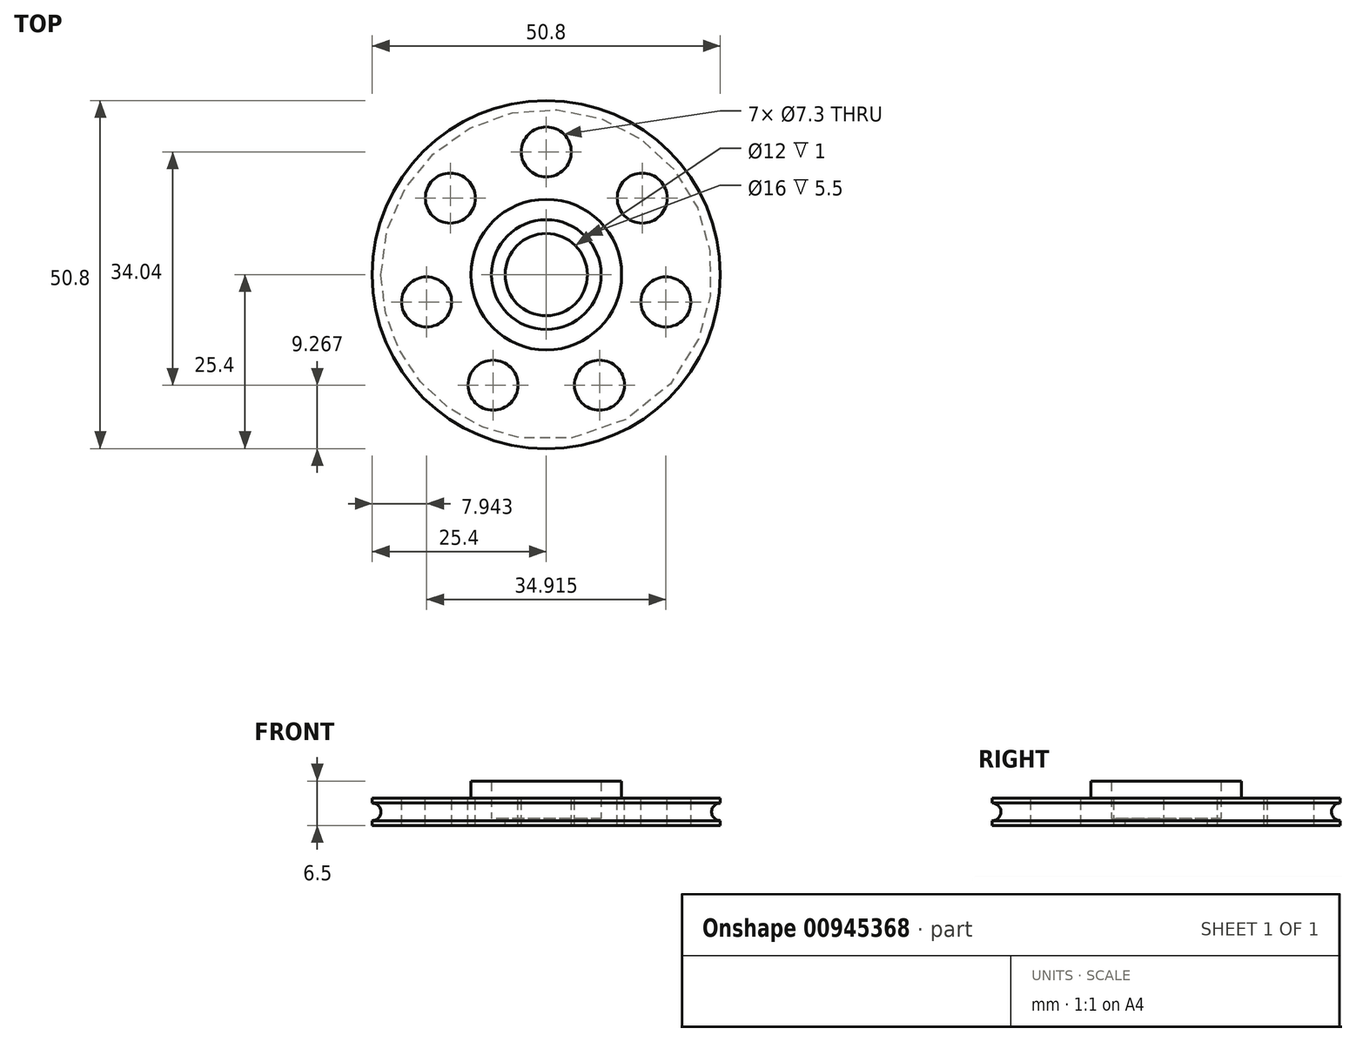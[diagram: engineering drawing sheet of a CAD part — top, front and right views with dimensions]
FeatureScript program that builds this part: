
annotation { "Feature Type Name" : "Feature", "Feature Type Description" : "" }
export const myFeature = defineFeature(function(context is Context, id is Id, definition is map)
    precondition{}
    {
        {
            var Q0;
            Q0=qCreatedBy(makeId("Top.planeOp"),FACE);
            var sketch = newSketch(context, id + "F0", { "sketchPlane" : qUnion([Q0])});
            skCircle(sketch, "E0", {"center": v(0, 0) * mm, "radius": 25.4 * mm});
            skSolve(sketch);
        }
        {
            var Q0;
            Q0=makeQuery(id+"F0.imprint","IMPRINT",FACE,{"disambiguationData":[TD([[makeQuery(id+"F0.imprint","IMPRINT",EDGE,{"derivedFrom":sQuery(id+"F0.wireOp",EDGE,"E0")}),1.0]])]});
            extrude(context, id + "F1", {"entities" : qUnion([Q0]), "depth" : 4 * mm, "offsetDistance" : 25.4 * mm});
        }
        {
            var Q0;
            Q0=makeQuery(id+"F1.opExtrude","CAP_FACE",FACE,{"disambiguationData":[OSD([sQuery(id+"F0.wireOp",EDGE,"E0"),sQuery(id+"F0.wireOp",EDGE,"n39IqKt5-bk1q-LU1x-fgod-8OyBNiFTd7FZ")])],"isStart":false});
            var sketch = newSketch(context, id + "F2", { "sketchPlane" : qUnion([Q0])});
            skCircle(sketch, "E1", {"center": v(0, 0) * mm, "radius": 8 * mm});
            skCircle(sketch, "E2.0", {"center": v(0, 0) * mm, "radius": 11 * mm});
            skSolve(sketch);
        }
        {
            var Q0;
            Q0=qSketchRegion(id+"F2",true);
            extrude(context, id + "F3", {"entities" : qUnion([Q0]), "operationType" : NewBodyOperationType.ADD, "flatOperationType" : FlatOperationType.REMOVE, "depth" : 2.5 * mm, "offsetDistance" : 25.4 * mm, "domain" : OperationDomain.MODEL});
        }
        {
            var Q0;
            Q0=makeQuery(id+"F3.boolean.opBoolean","SPLIT",FACE,{"disambiguationData":[TD([makeQuery(id+"F3.opExtrude","SWEPT_FACE",FACE,{"disambiguationData":[OSD([sQuery(id+"F2.wireOp",EDGE,"E1")])]})])],"derivedFrom":makeQuery(id+"F1.opExtrude","CAP_FACE",FACE,{"disambiguationData":[OSD([sQuery(id+"F0.wireOp",EDGE,"E0")])],"isStart":false})});
            var sketch = newSketch(context, id + "F4", { "sketchPlane" : qUnion([Q0])});
            skCircle(sketch, "E3", {"center": v(0, 0) * mm, "radius": 6 * mm});
            skSolve(sketch);
        }
        {
            var Q0;
            Q0=makeQuery(id+"F4.imprint","IMPRINT",FACE,{"disambiguationData":[TD([[makeQuery(id+"F4.imprint","IMPRINT",EDGE,{"derivedFrom":sQuery(id+"F4.wireOp",EDGE,"E3")}),1.0]])]});
            var Q1;
            Q1=makeQuery(id+"F4.imprint","IMPRINT",FACE,{"disambiguationData":[TD([[makeQuery(id+"F4.imprint","IMPRINT",EDGE,{"derivedFrom":makeQuery(id+"FgYK8jIepfClWtA_1.opExtrude","CAP_EDGE",EDGE,{"disambiguationData":[OSD([sQuery(id+"F8DXjnVyigKkjng_1.wireOp",EDGE,"EUjAMsCd-Zx2B-3j4q-cP5o-T3GrjTijNDqK")])],"isStart":false})}),1.0]])]});
            extrude(context, id + "F5", {"entities" : qUnion([Q0, Q1]), "operationType" : NewBodyOperationType.REMOVE, "oppositeDirection" : true, "depth" : 9 * mm, "offsetDistance" : 25.4 * mm});
        }
        {
            var Q0;
            Q0=qCreatedBy(makeId("Front.planeOp"),FACE);
            var sketch = newSketch(context, id + "F6", { "sketchPlane" : qUnion([Q0])});
            skCircle(sketch, "E4", {"center": v(-27.3, 2) * mm, "radius": 1.5 * mm});
            skLineSegment(sketch, "E5.bottom", {"start": v(-25.8, 0.65) * mm, "end": v(-27.95, 0.65) * mm});
            skLineSegment(sketch, "E5.top", {"start": v(-25.8, 3.35) * mm, "end": v(-27.95, 3.35) * mm});
            skLineSegment(sketch, "E5.left", {"start": v(-25.8, 0.65) * mm, "end": v(-25.8, 3.35) * mm});
            skLineSegment(sketch, "E5.right", {"start": v(-28.8, 1.91) * mm, "end": v(-28.8, 2.09) * mm});
            skLineSegment(sketch, "E6", {"start": v(0, 19.1) * mm, "end": v(0, -12.61) * mm, "construction": true});
            skLineSegment(sketch, "E7", {"start": v(-25.8, 1.83) * mm, "end": v(-25.81, 1.83) * mm});
            skPoint(sketch, "E8.orphan", {"position": v(-38.97, 3.35) * mm});
            skPoint(sketch, "E9.end.orphan", {"position": v(-15.64, 0.65) * mm});
            skPoint(sketch, "E9.start.orphan", {"position": v(-25.8, 2) * mm});
            skSolve(sketch);
        }
        {
            var Q0;
            {var subQ0=sQuery(id+"F6.wireOp",EDGE,"E5.top");var subQ1=sQuery(id+"F6.wireOp",EDGE,"E4");var subQ2=makeQuery(id+"F6.imprint","INTERSECT",VERTEX,{"disambiguationData":[OD(0.0)],"derivedFrom":[subQ1,subQ0]});Q0=makeQuery(id+"F6.imprint","IMPRINT",FACE,{"disambiguationData":[TD([[makeQuery(id+"F6.imprint","IMPRINT",EDGE,{"disambiguationData":[TD([[subQ2,1.0]])],"derivedFrom":subQ1}),1.0]])]});}
            var Q1;
            {var subQ0=sQuery(id+"F6.wireOp",EDGE,"E5.bottom");var subQ1=sQuery(id+"F6.wireOp",EDGE,"E4");var subQ2=makeQuery(id+"F6.imprint","INTERSECT",VERTEX,{"disambiguationData":[OD(0.0)],"derivedFrom":[subQ1,subQ0]});Q1=makeQuery(id+"F6.imprint","IMPRINT",FACE,{"disambiguationData":[TD([[makeQuery(id+"F6.imprint","IMPRINT",EDGE,{"disambiguationData":[TD([[subQ2,-1.0]])],"derivedFrom":subQ1}),1.0]])]});}
            var Q2;
            {var subQ4=sQuery(id+"F6.wireOp",EDGE,"E5.right");Q2=makeQuery(id+"F6.imprint","IMPRINT",FACE,{"disambiguationData":[TD([[makeQuery(id+"F6.imprint","IMPRINT",EDGE,{"derivedFrom":subQ4}),-1.0]])]});}
            var Q3;
            {var subQ0=sQuery(id+"F6.wireOp",EDGE,"p3G3spWP-JurA-dj01-Cwvm-HHlCDoPDIoxd");Q3=makeQuery(id+"F6.imprint","IMPRINT",FACE,{"disambiguationData":[TD([[makeQuery(id+"F6.imprint","IMPRINT",EDGE,{"derivedFrom":subQ0}),1.0]])]});}
            var Q4;
            Q4=makeQuery(id+"F6.imprint","IMPRINT",FACE,{"disambiguationData":[TD([[makeQuery(id+"F6.imprint","IMPRINT",EDGE,{"derivedFrom":sQuery(id+"F6.wireOp",EDGE,"p3G3spWP-JurA-dj01-Cwvm-HHlCDoPDIoxd")}),-1.0]])]});
            var Q5;
            {var subQ0=sQuery(id+"F6.wireOp",EDGE,"E9");Q5=makeQuery(id+"F6.imprint","IMPRINT",FACE,{"disambiguationData":[TD([[makeQuery(id+"F6.imprint","IMPRINT",EDGE,{"derivedFrom":subQ0}),1.0]])]});}
            var Q6;
            Q6=sQuery(id+"F6.wireOp",EDGE,"E6");
            revolve(context, id + "F7", {"operationType" : NewBodyOperationType.REMOVE, "surfaceOperationType" : NewSurfaceOperationType.NEW, "entities" : qUnion([Q0, Q1, Q2, Q3, Q4, Q5]), "axis" : qUnion([Q6]), "revolveType" : RevolveType.FULL, "oppositeDirection" : true});
        }
        {
            var Q0;
            Q0=makeQuery(id+"F3.boolean.opBoolean","SPLIT",FACE,{"disambiguationData":[TD([makeQuery(id+"F3.opExtrude","SWEPT_FACE",FACE,{"disambiguationData":[OSD([sQuery(id+"F2.wireOp",EDGE,"E1")])]})])],"derivedFrom":makeQuery(id+"F1.opExtrude","CAP_FACE",FACE,{"disambiguationData":[OSD([sQuery(id+"F0.wireOp",EDGE,"E0")])],"isStart":false})});
            extrude(context, id + "F8", {"entities" : qUnion([Q0]), "operationType" : NewBodyOperationType.REMOVE, "oppositeDirection" : true, "depth" : 3 * mm, "offsetDistance" : 25 * mm});
        }
        {
            var Q0;
            Q0=qCreatedBy(makeId("Front.planeOp"),FACE);
            var sketch = newSketch(context, id + "F9", { "sketchPlane" : qUnion([Q0])});
            skLineSegment(sketch, "E10", {"start": v(-25.4, 4) * mm, "end": v(-25.4, 0) * mm});
            skCircle(sketch, "E11", {"center": v(-25.4, 2) * mm, "radius": 1.28 * mm});
            skLineSegment(sketch, "E12", {"start": v(0, 9.34) * mm, "end": v(0, -3.6) * mm, "construction": true});
            skSolve(sketch);
        }
        {
            var Q0;
            {var subQ0=sQuery(id+"F9.wireOp",EDGE,"E11");var subQ1=sQuery(id+"F9.wireOp",EDGE,"E10");var subQ2=makeQuery(id+"F9.imprint","INTERSECT",VERTEX,{"disambiguationData":[OD(0.0)],"derivedFrom":[subQ1,subQ0]});Q0=makeQuery(id+"F9.imprint","IMPRINT",FACE,{"disambiguationData":[TD([[makeQuery(id+"F9.imprint","IMPRINT",EDGE,{"disambiguationData":[TD([[subQ2,1.0]])],"derivedFrom":subQ1}),1.0]])]});}
            var Q1;
            {var subQ0=sQuery(id+"F9.wireOp",EDGE,"E11");var subQ1=sQuery(id+"F9.wireOp",EDGE,"E10");var subQ2=makeQuery(id+"F9.imprint","INTERSECT",VERTEX,{"disambiguationData":[OD(0.0)],"derivedFrom":[subQ1,subQ0]});Q1=makeQuery(id+"F9.imprint","IMPRINT",FACE,{"disambiguationData":[TD([[makeQuery(id+"F9.imprint","IMPRINT",EDGE,{"disambiguationData":[TD([[subQ2,1.0]])],"derivedFrom":subQ1}),-1.0]])]});}
            var Q2;
            Q2=sQuery(id+"F9.wireOp",EDGE,"E12");
            revolve(context, id + "F10", {"operationType" : NewBodyOperationType.REMOVE, "surfaceOperationType" : NewSurfaceOperationType.NEW, "entities" : qUnion([Q0, Q1]), "axis" : qUnion([Q2]), "revolveType" : RevolveType.FULL, "oppositeDirection" : true});
        }
        {
            var Q0;
            {var subQ1=sQuery(id+"F0.wireOp",EDGE,"E0");var subQ2=makeQuery(id+"F1.opExtrude","SWEPT_FACE",FACE,{"disambiguationData":[OSD([subQ1])]});Q0=makeQuery(id+"FvaswZWDLJZ7FP9_1.boolean.opBoolean","SPLIT",FACE,{"disambiguationData":[TD([subQ2])],"derivedFrom":makeQuery(id+"F3.boolean.opBoolean","SPLIT",FACE,{"disambiguationData":[TD([subQ2])],"derivedFrom":makeQuery(id+"F1.opExtrude","CAP_FACE",FACE,{"disambiguationData":[OSD([subQ1])],"isStart":false})})});}
            var sketch = newSketch(context, id + "F11", { "sketchPlane" : qUnion([Q0])});
            skCircle(sketch, "E13", {"center": v(0, 17.9) * mm, "radius": 3.65 * mm});
            skCircle(sketch, "E14.1.0", {"center": v(-14, 11.16) * mm, "radius": 3.65 * mm});
            skCircle(sketch, "E14.2.0", {"center": v(-17.46, -3.98) * mm, "radius": 3.65 * mm});
            skCircle(sketch, "E14.3.0", {"center": v(-7.77, -16.13) * mm, "radius": 3.65 * mm});
            skCircle(sketch, "E14.4.0", {"center": v(7.77, -16.13) * mm, "radius": 3.65 * mm});
            skPoint(sketch, "E14.center", {"position": v(0, 0) * mm});
            skCircle(sketch, "E15.1.5.0", {"center": v(17.46, -3.98) * mm, "radius": 3.65 * mm});
            skCircle(sketch, "E15.1.6.0", {"center": v(14, 11.16) * mm, "radius": 3.65 * mm});
            skSolve(sketch);
        }
        {
            var Q0;
            Q0=makeQuery(id+"F11.imprint","IMPRINT",FACE,{"disambiguationData":[TD([[makeQuery(id+"F11.imprint","IMPRINT",EDGE,{"derivedFrom":sQuery(id+"F11.wireOp",EDGE,"E13")}),1.0]])]});
            var Q1;
            Q1=makeQuery(id+"F11.imprint","IMPRINT",FACE,{"disambiguationData":[TD([[makeQuery(id+"F11.imprint","IMPRINT",EDGE,{"derivedFrom":sQuery(id+"F11.wireOp",EDGE,"E14.1.0")}),1.0]])]});
            var Q2;
            Q2=makeQuery(id+"F11.imprint","IMPRINT",FACE,{"disambiguationData":[TD([[makeQuery(id+"F11.imprint","IMPRINT",EDGE,{"derivedFrom":sQuery(id+"F11.wireOp",EDGE,"E14.2.0")}),1.0]])]});
            var Q3;
            Q3=makeQuery(id+"F11.imprint","IMPRINT",FACE,{"disambiguationData":[TD([[makeQuery(id+"F11.imprint","IMPRINT",EDGE,{"derivedFrom":sQuery(id+"F11.wireOp",EDGE,"E14.3.0")}),1.0]])]});
            var Q4;
            Q4=makeQuery(id+"F11.imprint","IMPRINT",FACE,{"disambiguationData":[TD([[makeQuery(id+"F11.imprint","IMPRINT",EDGE,{"derivedFrom":sQuery(id+"F11.wireOp",EDGE,"E14.4.0")}),1.0]])]});
            var Q5;
            Q5=makeQuery(id+"F11.imprint","IMPRINT",FACE,{"disambiguationData":[TD([[makeQuery(id+"F11.imprint","IMPRINT",EDGE,{"derivedFrom":sQuery(id+"F11.wireOp",EDGE,"E15.1.6.0")}),1.0]])]});
            var Q6;
            Q6=makeQuery(id+"F11.imprint","IMPRINT",FACE,{"disambiguationData":[TD([[makeQuery(id+"F11.imprint","IMPRINT",EDGE,{"derivedFrom":sQuery(id+"F11.wireOp",EDGE,"E15.1.5.0")}),1.0]])]});
            extrude(context, id + "F12", {"entities" : qUnion([Q0, Q1, Q2, Q3, Q4, Q5, Q6]), "operationType" : NewBodyOperationType.REMOVE, "oppositeDirection" : true, "depth" : 25 * mm, "offsetDistance" : 25 * mm});
        }
    });
